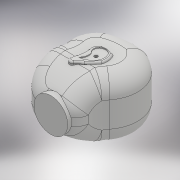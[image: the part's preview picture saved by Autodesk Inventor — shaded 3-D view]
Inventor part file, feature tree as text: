
AUTODESK INVENTOR PART (.ipt)
format: ipt  version: 2017 (Build 210142000, 142)  size: 1,234,432 bytes
history: native  units: mm
features: extrude x14, sketch x14, fillet x4, projected_geometry x4, shell x1, mirror x1
ambient origin geometry x8: Origin, YZ Plane, XZ Plane, XY Plane, X Axis, Y Axis, Z Axis, Center Point
bodies: Solid1 (feature_tree)
feature tree (38):
  extrude  "Extrusion1"  Depth=1.0mm TaperAngle=0.0deg
  extrude  "Extrusion2"  Depth=14.99mm
  fillet  "Fillet1"  Radius=72.0mm
  fillet  "Fillet2"  Radius=14.99mm
  extrude  "Extrusion3"  Depth=1.0mm TaperAngle=0.0deg
  fillet  "Fillet3"  Radius=3.0mm
  shell  "Shell2"  Thickness=1.0mm
  extrude  "Extrusion4"  Depth=2.0mm TaperAngle=0.0deg
  extrude  "Extrusion5"  Depth=1.5mm TaperAngle=0.0deg
  extrude  "Extrusion6"  Depth=4.0mm TaperAngle=0.0deg
  extrude  "Extrusion7"  Depth=0.5mm TaperAngle=0.0deg
  extrude  "Extrusion8"  Depth=10.0mm
  extrude  "Extrusion9"  [1 undecoded]
  extrude  "Extrusion11"  [1 undecoded]
  fillet  "Fillet4"  [1 undecoded]
  extrude  "Extrusion12"  [1 undecoded]
  extrude  "Extrusion13"  [1 undecoded]
  extrude  "Extrusion14"  [1 undecoded]
  mirror  "Mirror4"
  extrude  "Extrusion15"  [1 undecoded]
  sketch  "Sketch1"  dims[d1=26.0mm d2=0.0mm d3=1.0mm d4=0.0mm]
  sketch  "Sketch2"  dims[d8=15.0mm d9=15.0mm d12=72.0mm d13=0.0mm d14=14.99mm]
  sketch  "Sketch6"  dims[d16=2.0mm d17=1.0mm d18=0.0mm]
  sketch  "Sketch7"  dims[d19=1.0mm d20=6.343mm d21=7.0mm d22=0.0mm d23=3.0mm d24=0.0mm d25=1.0mm]
  sketch  "Sketch8"  dims[d26=6.0mm d27=0.0mm d28=2.0mm d29=0.0mm]
  sketch  "Sketch10"  dims[d30=3.0mm d31=0.0mm d34=1.5mm d35=0.0mm]
  sketch  "Sketch11"  dims[d36=1.5mm d38=4.0mm d39=0.0mm]
  projected_geometry  "Projected Loop1"
  sketch  "Sketch12"  dims[d40=0.5mm d41=0.0mm d42=0.5mm d43=0.0mm]
  projected_geometry  "Projected Loop2"
  sketch  "Sketch13"  dims[d45=10.0mm d46=0.0mm d47=29.25mm]
  sketch  "Sketch15"
  projected_geometry  "Projected Loop4"
  projected_geometry  "Projected Loop5"
  sketch  "Sketch16"
  sketch  "Sketch17"
  sketch  "Sketch18"
  sketch  "Sketch19"
note: 7 required parameter values undecoded (feature->parameter linkage not recoverable at this tier; creation-order binding heuristic only, values carry confidence <= 0.55)
